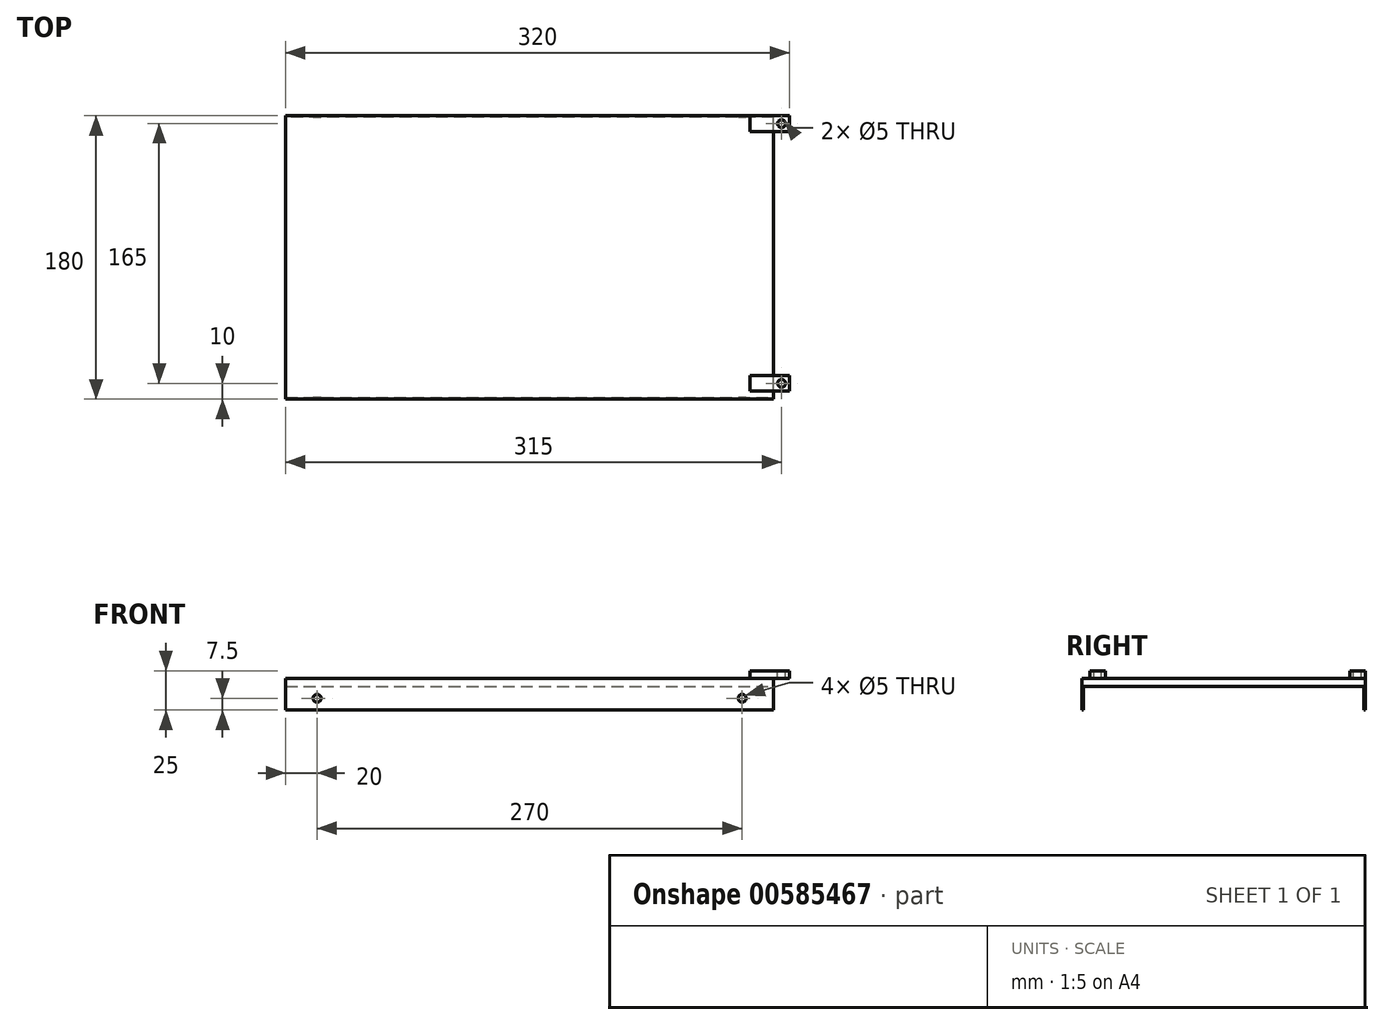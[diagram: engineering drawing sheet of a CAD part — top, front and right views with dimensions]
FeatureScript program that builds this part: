
annotation { "Feature Type Name" : "Feature", "Feature Type Description" : "" }
export const myFeature = defineFeature(function(context is Context, id is Id, definition is map)
    precondition{}
    {
        {
            var Q0;
            Q0=qCreatedBy(makeId("Top.planeOp"),FACE);
            var sketch = newSketch(context, id + "F0", { "sketchPlane" : qUnion([Q0])});
            skLineSegment(sketch, "E0.bottom", {"start": v(155, -90) * mm, "end": v(-155, -90) * mm});
            skLineSegment(sketch, "E0.top", {"start": v(155, 90) * mm, "end": v(-155, 90) * mm});
            skLineSegment(sketch, "E0.left", {"start": v(155, -90) * mm, "end": v(155, 90) * mm});
            skLineSegment(sketch, "E0.right", {"start": v(-155, -90) * mm, "end": v(-155, 90) * mm});
            skPoint(sketch, "E0.middle", {"position": v(0, 0) * mm});
            skSolve(sketch);
        }
        {
            var Q0;
            Q0 = qSketchRegion(id + "F0", true);
            extrude(context, id + "F1", {"entities" : qUnion([Q0]), "depth" : 5 * mm, "offsetDistance" : 25 * mm});
        }
        {
            var Q0;
            Q0=makeQuery(id+"F1.opExtrude","CAP_FACE",FACE,{"disambiguationData":[OSD([sQuery(id+"F0.wireOp",EDGE,"E0.bottom"),sQuery(id+"F0.wireOp",EDGE,"E0.top"),sQuery(id+"F0.wireOp",EDGE,"E0.left"),sQuery(id+"F0.wireOp",EDGE,"E0.right")])],"isStart":false});
            var sketch = newSketch(context, id + "F2", { "sketchPlane" : qUnion([Q0])});
            skLineSegment(sketch, "E1.bottom", {"start": v(140, 90) * mm, "end": v(165, 90) * mm});
            skLineSegment(sketch, "E1.top", {"start": v(140, 80) * mm, "end": v(165, 80) * mm});
            skLineSegment(sketch, "E1.left", {"start": v(140, 90) * mm, "end": v(140, 80) * mm});
            skLineSegment(sketch, "E1.right", {"start": v(165, 90) * mm, "end": v(165, 80) * mm});
            skSolve(sketch);
        }
        {
            var Q0;
            Q0 = qSketchRegion(id + "F2", true);
            extrude(context, id + "F3", {"entities" : qUnion([Q0]), "operationType" : NewBodyOperationType.ADD, "depth" : 5 * mm, "offsetDistance" : 25 * mm});
        }
        {
            var Q0;
            Q0=makeQuery(id+"F3.opExtrude","CAP_FACE",FACE,{"disambiguationData":[OSD([sQuery(id+"F2.wireOp",EDGE,"E1.bottom"),sQuery(id+"F2.wireOp",EDGE,"E1.top"),sQuery(id+"F2.wireOp",EDGE,"E1.left"),sQuery(id+"F2.wireOp",EDGE,"E1.right")])],"isStart":false});
            var sketch = newSketch(context, id + "F4", { "sketchPlane" : qUnion([Q0])});
            skLineSegment(sketch, "E2", {"start": v(165, 85) * mm, "end": v(160, 85) * mm});
            skSolve(sketch);
        }
        {
            var Q0;
            Q0=sQuery(id+"F4.wireOp",VERTEX,"E2.end");
            var Q1;
            Q1=makeQuery(id+"F1.opExtrude","SWEPT_BODY",BODY,{"disambiguationData":[OSD([sQuery(id+"F0.wireOp",EDGE,"E0.bottom"),sQuery(id+"F0.wireOp",EDGE,"E0.top"),sQuery(id+"F0.wireOp",EDGE,"E0.left"),sQuery(id+"F0.wireOp",EDGE,"E0.right")])]});
            hole(context, id + "F5", {"style" : HoleStyle.SIMPLE, "endStyle" : HoleEndStyle.THROUGH, "holeDiameter" : 5 * mm, "majorDiameter" : 5 * mm, "isTappedThrough" : true, "tappedDepth" : 12 * mm, "tapClearance" : 3, "locations" : qUnion([Q0]), "scope" : qUnion([Q1])});
        }
        {
            var Q0;
            Q0=makeQuery(id+"F1.opExtrude","CAP_FACE",FACE,{"disambiguationData":[OSD([sQuery(id+"F0.wireOp",EDGE,"E0.bottom"),sQuery(id+"F0.wireOp",EDGE,"E0.top"),sQuery(id+"F0.wireOp",EDGE,"E0.left"),sQuery(id+"F0.wireOp",EDGE,"E0.right")])],"isStart":false});
            var sketch = newSketch(context, id + "F6", { "sketchPlane" : qUnion([Q0])});
            skLineSegment(sketch, "E3.bottom", {"start": v(140, -85) * mm, "end": v(165, -85) * mm});
            skLineSegment(sketch, "E3.top", {"start": v(140, -75) * mm, "end": v(165, -75) * mm});
            skLineSegment(sketch, "E3.left", {"start": v(140, -85) * mm, "end": v(140, -75) * mm});
            skLineSegment(sketch, "E3.right", {"start": v(165, -85) * mm, "end": v(165, -75) * mm});
            skSolve(sketch);
        }
        {
            var Q0;
            Q0 = qSketchRegion(id + "F6", true);
            extrude(context, id + "F7", {"entities" : qUnion([Q0]), "operationType" : NewBodyOperationType.ADD, "depth" : 5 * mm, "offsetDistance" : 25 * mm});
        }
        {
            var Q0;
            Q0=makeQuery(id+"F7.opExtrude","CAP_FACE",FACE,{"disambiguationData":[OSD([sQuery(id+"F6.wireOp",EDGE,"E3.bottom"),sQuery(id+"F6.wireOp",EDGE,"E3.top"),sQuery(id+"F6.wireOp",EDGE,"E3.left"),sQuery(id+"F6.wireOp",EDGE,"E3.right")])],"isStart":false});
            var sketch = newSketch(context, id + "F8", { "sketchPlane" : qUnion([Q0])});
            skLineSegment(sketch, "E4", {"start": v(165, -80) * mm, "end": v(160, -80) * mm});
            skSolve(sketch);
        }
        {
            var Q0;
            Q0=sQuery(id+"F8.wireOp",VERTEX,"E4.end");
            var Q1;
            Q1=makeQuery(id+"F1.opExtrude","SWEPT_BODY",BODY,{"disambiguationData":[OSD([sQuery(id+"F0.wireOp",EDGE,"E0.bottom"),sQuery(id+"F0.wireOp",EDGE,"E0.top"),sQuery(id+"F0.wireOp",EDGE,"E0.left"),sQuery(id+"F0.wireOp",EDGE,"E0.right")])]});
            hole(context, id + "F9", {"style" : HoleStyle.SIMPLE, "endStyle" : HoleEndStyle.THROUGH, "holeDiameter" : 5 * mm, "majorDiameter" : 5 * mm, "isTappedThrough" : true, "tappedDepth" : 12 * mm, "tapClearance" : 3, "locations" : qUnion([Q0]), "scope" : qUnion([Q1])});
        }
        {
            var Q0;
            Q0=makeQuery(id+"F1.opExtrude","CAP_FACE",FACE,{"disambiguationData":[OSD([sQuery(id+"F0.wireOp",EDGE,"E0.bottom"),sQuery(id+"F0.wireOp",EDGE,"E0.top"),sQuery(id+"F0.wireOp",EDGE,"E0.left"),sQuery(id+"F0.wireOp",EDGE,"E0.right")])],"isStart":true});
            var sketch = newSketch(context, id + "F10", { "sketchPlane" : qUnion([Q0])});
            skLineSegment(sketch, "E5.bottom", {"start": v(155, -90) * mm, "end": v(-155, -90) * mm});
            skLineSegment(sketch, "E5.top", {"start": v(155, -89) * mm, "end": v(-155, -89) * mm});
            skLineSegment(sketch, "E5.left", {"start": v(155, -90) * mm, "end": v(155, -89) * mm});
            skLineSegment(sketch, "E5.right", {"start": v(-155, -90) * mm, "end": v(-155, -89) * mm});
            skLineSegment(sketch, "E6.bottom", {"start": v(-155, 90) * mm, "end": v(155, 90) * mm});
            skLineSegment(sketch, "E6.top", {"start": v(-155, 89) * mm, "end": v(155, 89) * mm});
            skLineSegment(sketch, "E6.left", {"start": v(-155, 90) * mm, "end": v(-155, 89) * mm});
            skLineSegment(sketch, "E6.right", {"start": v(155, 90) * mm, "end": v(155, 89) * mm});
            skSolve(sketch);
        }
        {
            var Q0;
            Q0=makeQuery(id+"F10.imprint","IMPRINT",FACE,{"disambiguationData":[TD([[makeQuery(id+"F10.imprint","IMPRINT",EDGE,{"derivedFrom":sQuery(id+"F10.wireOp",EDGE,"E5.bottom")}),-1.0]])]});
            var Q1;
            Q1=makeQuery(id+"F10.imprint","IMPRINT",FACE,{"disambiguationData":[TD([[makeQuery(id+"F10.imprint","IMPRINT",EDGE,{"derivedFrom":sQuery(id+"F10.wireOp",EDGE,"E6.bottom")}),1.0]])]});
            extrude(context, id + "F11", {"entities" : qUnion([Q0, Q1]), "operationType" : NewBodyOperationType.ADD, "depth" : 15 * mm, "offsetDistance" : 25 * mm});
        }
        {
            var Q0;
            Q0=makeQuery(id+"F11.boolean.opBoolean","MERGE",FACE,{"derivedFrom":[makeQuery(id+"F3.boolean.opBoolean","MERGE",FACE,{"derivedFrom":[makeQuery(id+"F1.opExtrude","SWEPT_FACE",FACE,{"disambiguationData":[OSD([sQuery(id+"F0.wireOp",EDGE,"E0.top")])]}),makeQuery(id+"F3.opExtrude","SWEPT_FACE",FACE,{"disambiguationData":[OSD([sQuery(id+"F2.wireOp",EDGE,"E1.bottom")])]})]}),makeQuery(id+"F11.opExtrude","SWEPT_FACE",FACE,{"disambiguationData":[OSD([sQuery(id+"F10.wireOp",EDGE,"E5.bottom")])]})]});
            var sketch = newSketch(context, id + "F12", { "sketchPlane" : qUnion([Q0])});
            skLineSegment(sketch, "E7", {"start": v(-135, -15) * mm, "end": v(-135, -7.5) * mm});
            skSolve(sketch);
        }
        {
            var Q0;
            Q0=sQuery(id+"F12.wireOp",VERTEX,"E7.end");
            var Q1;
            Q1=makeQuery(id+"F1.opExtrude","SWEPT_BODY",BODY,{"disambiguationData":[OSD([sQuery(id+"F0.wireOp",EDGE,"E0.bottom"),sQuery(id+"F0.wireOp",EDGE,"E0.top"),sQuery(id+"F0.wireOp",EDGE,"E0.left"),sQuery(id+"F0.wireOp",EDGE,"E0.right")])]});
            hole(context, id + "F13", {"style" : HoleStyle.SIMPLE, "endStyle" : HoleEndStyle.THROUGH, "holeDiameter" : 5 * mm, "majorDiameter" : 5 * mm, "isTappedThrough" : true, "tappedDepth" : 12 * mm, "tapClearance" : 3, "locations" : qUnion([Q0]), "scope" : qUnion([Q1])});
        }
        {
            var Q0;
            Q0=makeQuery(id+"F11.boolean.opBoolean","MERGE",FACE,{"derivedFrom":[makeQuery(id+"F3.boolean.opBoolean","MERGE",FACE,{"derivedFrom":[makeQuery(id+"F1.opExtrude","SWEPT_FACE",FACE,{"disambiguationData":[OSD([sQuery(id+"F0.wireOp",EDGE,"E0.top")])]}),makeQuery(id+"F3.opExtrude","SWEPT_FACE",FACE,{"disambiguationData":[OSD([sQuery(id+"F2.wireOp",EDGE,"E1.bottom")])]})]}),makeQuery(id+"F11.opExtrude","SWEPT_FACE",FACE,{"disambiguationData":[OSD([sQuery(id+"F10.wireOp",EDGE,"E5.bottom")])]})]});
            var sketch = newSketch(context, id + "F14", { "sketchPlane" : qUnion([Q0])});
            skLineSegment(sketch, "E8", {"start": v(135, -15) * mm, "end": v(135, -7.5) * mm});
            skSolve(sketch);
        }
        {
            var Q0;
            Q0=sQuery(id+"F14.wireOp",VERTEX,"E8.end");
            var Q1;
            Q1=makeQuery(id+"F1.opExtrude","SWEPT_BODY",BODY,{"disambiguationData":[OSD([sQuery(id+"F0.wireOp",EDGE,"E0.bottom"),sQuery(id+"F0.wireOp",EDGE,"E0.top"),sQuery(id+"F0.wireOp",EDGE,"E0.left"),sQuery(id+"F0.wireOp",EDGE,"E0.right")])]});
            hole(context, id + "F15", {"style" : HoleStyle.SIMPLE, "endStyle" : HoleEndStyle.THROUGH, "holeDiameter" : 5 * mm, "majorDiameter" : 5 * mm, "isTappedThrough" : true, "tappedDepth" : 12 * mm, "tapClearance" : 3, "locations" : qUnion([Q0]), "scope" : qUnion([Q1])});
        }
    });
